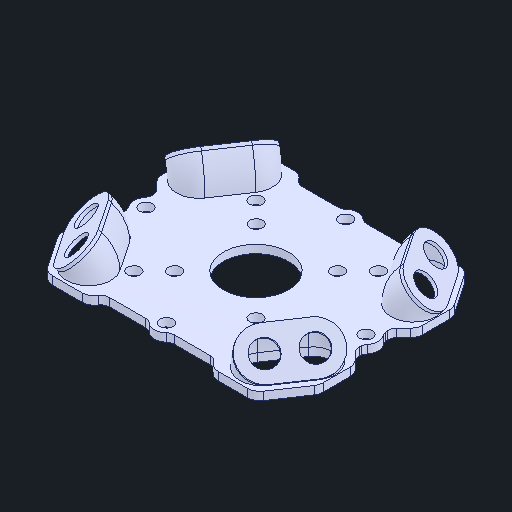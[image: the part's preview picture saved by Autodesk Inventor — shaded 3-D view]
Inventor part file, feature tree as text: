
AUTODESK INVENTOR PART (.ipt)
format: ipt  version: 2023 (Build 270158000, 158)  size: 406,528 bytes
history: native  units: in
note: dims shown in document units (in); Inventor stores cm internally (conversion verified against a paired STEP export)
features: fillet x1
ambient origin geometry x8: Origin, YZ Plane, XZ Plane, XY Plane, X Axis, Y Axis, Z Axis, Center Point
bodies: Solid1 (feature_tree)
feature tree (1):
  fillet  "Fillet3"  [1 undecoded]
note: 1 required parameter value undecoded (feature->parameter linkage not recoverable at this tier; creation-order binding heuristic only, values carry confidence <= 0.55)
